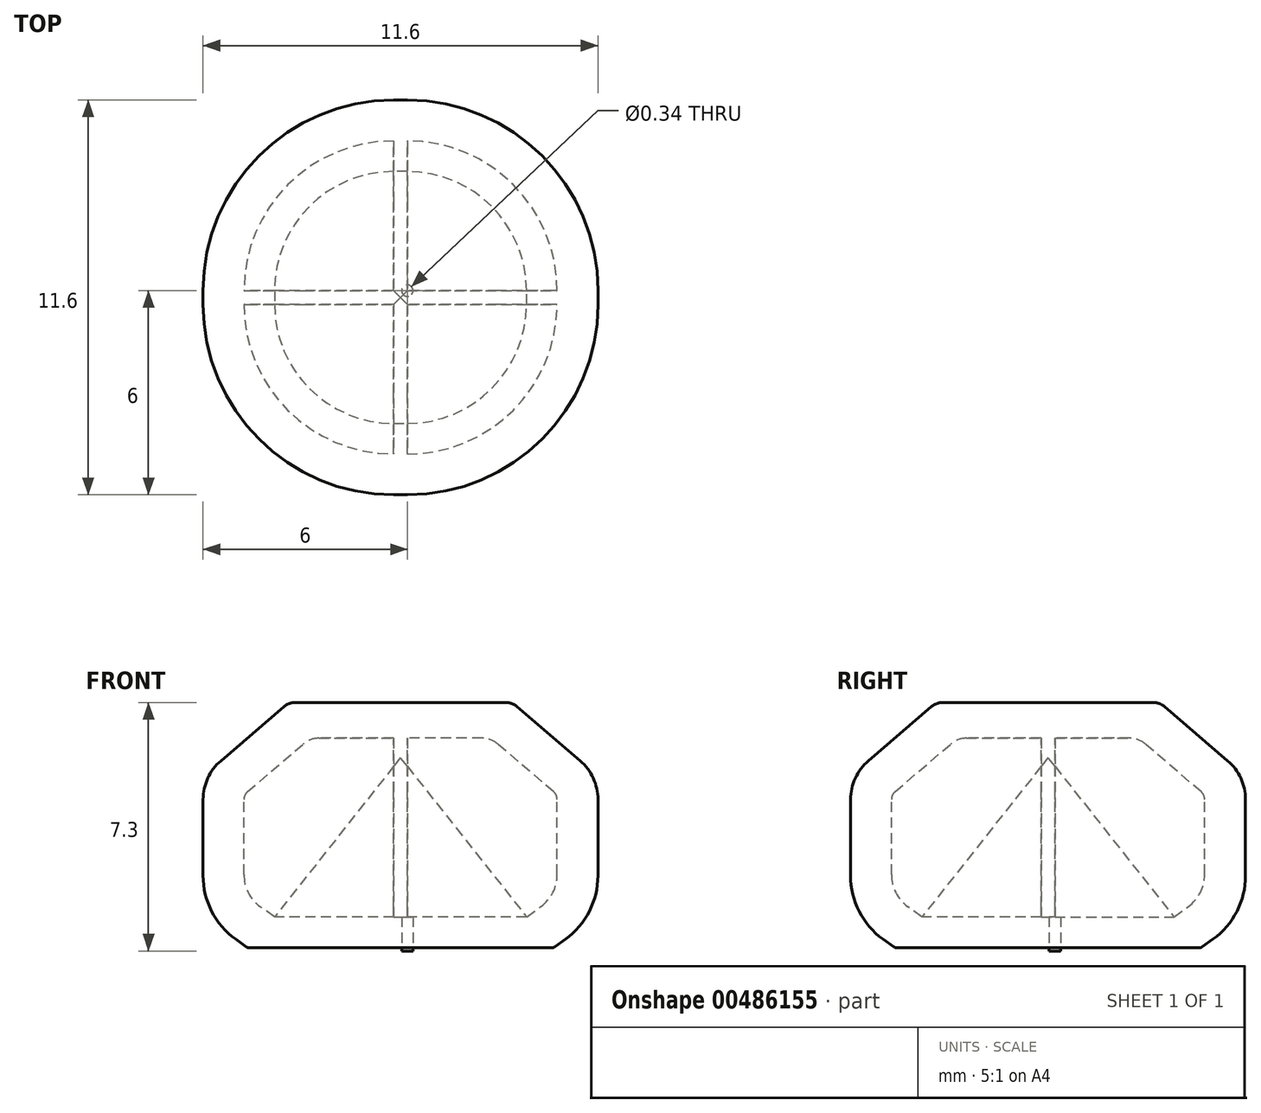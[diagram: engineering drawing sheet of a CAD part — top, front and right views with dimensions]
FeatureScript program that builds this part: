
annotation { "Feature Type Name" : "Feature", "Feature Type Description" : "" }
export const myFeature = defineFeature(function(context is Context, id is Id, definition is map)
    precondition{}
    {
        {
            assignVariable(context, id + "F0", {"name" : "l2", "anyValue" : 0.4});
        }
        {
            assignVariable(context, id + "F1", {"name" : "Scaf", "anyValue" : 0.65});
        }
        {
            var Q0;
            Q0=qCreatedBy(makeId("Front.planeOp"),FACE);
            var sketch = newSketch(context, id + "F2", { "sketchPlane" : qUnion([Q0])});
            skLineSegment(sketch, "E0", {"start": v(0, 0) * mm, "end": v(4.27, 0) * mm});
            skLineSegment(sketch, "E1", {"start": v(5.6, 2.11) * mm, "end": v(5.6, 4.35) * mm});
            skLineSegment(sketch, "E2", {"start": v(2.9, 7.2) * mm, "end": v(0, 7.2) * mm});
            skLineSegment(sketch, "E3", {"start": v(4.33, 0.02) * mm, "end": v(4.65, 0.25) * mm});
            skLineSegment(sketch, "E4", {"start": v(5.08, 5.49) * mm, "end": v(3.22, 7.08) * mm});
            skLineSegment(sketch, "E5", {"start": v(0, 0) * mm, "end": v(0, 0.9) * mm});
            skLineSegment(sketch, "E6", {"start": v(0, 0.9) * mm, "end": v(3.5, 0.9) * mm});
            skLineSegment(sketch, "E7", {"start": v(4.4, 2.14) * mm, "end": v(4.4, 4.35) * mm});
            skLineSegment(sketch, "E8", {"start": v(4.3, 4.58) * mm, "end": v(2.66, 5.98) * mm});
            skLineSegment(sketch, "E9", {"start": v(2.2, 6.15) * mm, "end": v(0, 6.15) * mm});
            skLineSegment(sketch, "E10", {"start": v(0, 6.15) * mm, "end": v(0, 7.2) * mm});
            skLineSegment(sketch, "E11", {"start": v(3.5, 0.9) * mm, "end": v(3.92, 1.2) * mm});
            skPoint(sketch, "E12.visualSharp", {"position": v(5.6, 0.94) * mm});
            skArc(sketch, "E12.filletArc", {"start": v(4.65, 0.25) * mm, "mid": v(5.35, 1.06) * mm, "end": v(5.6, 2.11) * mm});
            skPoint(sketch, "E13.visualSharp", {"position": v(5.6, 5.04) * mm});
            skArc(sketch, "E13.filletArc", {"start": v(5.6, 4.35) * mm, "mid": v(5.46, 4.98) * mm, "end": v(5.08, 5.49) * mm});
            skPoint(sketch, "E14.visualSharp", {"position": v(3.08, 7.2) * mm});
            skArc(sketch, "E14.filletArc", {"start": v(3.22, 7.08) * mm, "mid": v(3.07, 7.17) * mm, "end": v(2.9, 7.2) * mm});
            skPoint(sketch, "E15.visualSharp", {"position": v(2.46, 6.15) * mm});
            skArc(sketch, "E15.filletArc", {"start": v(2.66, 5.98) * mm, "mid": v(2.45, 6.1) * mm, "end": v(2.2, 6.15) * mm});
            skPoint(sketch, "E16.visualSharp", {"position": v(4.4, 4.49) * mm});
            skArc(sketch, "E16.filletArc", {"start": v(4.4, 4.35) * mm, "mid": v(4.37, 4.48) * mm, "end": v(4.3, 4.58) * mm});
            skPoint(sketch, "E17.visualSharp", {"position": v(4.4, 1.55) * mm});
            skArc(sketch, "E17.filletArc", {"start": v(3.92, 1.2) * mm, "mid": v(4.27, 1.61) * mm, "end": v(4.4, 2.14) * mm});
            skPoint(sketch, "E18.visualSharp", {"position": v(4.3, 0) * mm});
            skArc(sketch, "E18.filletArc", {"start": v(4.27, 0) * mm, "mid": v(4.3, 0) * mm, "end": v(4.33, 0.02) * mm});
            skSolve(sketch);
        }
        {
            var Q0;
            Q0=makeQuery(id+"F2.imprint","IMPRINT",FACE,{"disambiguationData":[TD([[makeQuery(id+"F2.imprint","IMPRINT",EDGE,{"derivedFrom":sQuery(id+"F2.wireOp",EDGE,"E0")}),1.0]])]});
            extrude(context, id + "F3", {"entities" : qUnion([Q0]), "depth" : (getVariable(context, 'l2')) * mm, "offsetDistance" : 25 * mm});
        }
        {
            var Q0;
            Q0=makeQuery(id+"F3.opExtrude","SWEPT_FACE",FACE,{"disambiguationData":[OSD([sQuery(id+"F2.wireOp",EDGE,"E10")])]});
            var Q1;
            Q1=sQuery(id+"F10.wireOp",EDGE,"E19");
            extrude(context, id + "F4", {"entities" : qUnion([Q0]), "operationType" : NewBodyOperationType.ADD, "surfaceEntities" : qUnion([Q1]), "depth" : (getVariable(context, 'Scaf')) * mm, "offsetDistance" : 25 * mm});
        }
        {
            var Q1;
            Q1=makeQuery(id+"F3.opExtrude","SWEPT_FACE",FACE,{"disambiguationData":[OSD([sQuery(id+"F2.wireOp",EDGE,"E9")])]});
            var Q2;
            Q2=makeQuery(id+"F3.opExtrude","SWEPT_FACE",FACE,{"disambiguationData":[OSD([sQuery(id+"F2.wireOp",EDGE,"E11")])]});
            loft(context, id + "F5", {"operationType" : NewBodyOperationType.ADD, "sheetProfilesArray" : [{ "sheetProfileEntities" : qUnion([Q1]) }, { "sheetProfileEntities" : qUnion([Q2]) }]});
        }
        {
            var Q1;
            Q1=makeQuery(id+"F3.opExtrude","SWEPT_FACE",FACE,{"disambiguationData":[OSD([sQuery(id+"F2.wireOp",EDGE,"E17.filletArc")])]});
            var Q2;
            Q2=makeQuery(id+"F3.opExtrude","SWEPT_FACE",FACE,{"disambiguationData":[OSD([sQuery(id+"F2.wireOp",EDGE,"E15.filletArc")])]});
            loft(context, id + "F6", {"operationType" : NewBodyOperationType.ADD, "sheetProfilesArray" : [{ "sheetProfileEntities" : qUnion([Q1]) }, { "sheetProfileEntities" : qUnion([Q2]) }]});
        }
        {
            var Q1;
            Q1=makeQuery(id+"F3.opExtrude","SWEPT_FACE",FACE,{"disambiguationData":[OSD([sQuery(id+"F2.wireOp",EDGE,"E8")])]});
            var Q2;
            Q2=makeQuery(id+"F3.opExtrude","SWEPT_FACE",FACE,{"disambiguationData":[OSD([sQuery(id+"F2.wireOp",EDGE,"E7")])]});
            loft(context, id + "F7", {"operationType" : NewBodyOperationType.ADD, "sheetProfilesArray" : [{ "sheetProfileEntities" : qUnion([Q1]) }, { "sheetProfileEntities" : qUnion([Q2]) }]});
        }
        {
            var Q0;
            Q0=makeQuery(id+"F7.opLoft","SWEPT_FACE",FACE,{"disambiguationData":[OSD([sQuery(id+"F2.wireOp",EDGE,"E7"),sQuery(id+"F2.wireOp",EDGE,"E8"),sQuery(id+"F2.wireOp",EDGE,"E16.filletArc")])]});
            extrude(context, id + "F8", {"entities" : qUnion([Q0]), "operationType" : NewBodyOperationType.ADD, "depth" : .2 * mm, "offsetDistance" : 25 * mm});
        }
        {
            var Q0;
            Q0=makeQuery(id+"F2.imprint","IMPRINT",FACE,{"disambiguationData":[TD([[makeQuery(id+"F2.imprint","IMPRINT",EDGE,{"derivedFrom":sQuery(id+"F2.wireOp",EDGE,"E0")}),1.0]])]});
            var Q1;
            Q1=sQuery(id+"F2.wireOp",EDGE,"E10");
            revolve(context, id + "F9", {"operationType" : NewBodyOperationType.ADD, "entities" : qUnion([Q0]), "axis" : qUnion([Q1]), "revolveType" : RevolveType.ONE_DIRECTION, "angle" : 90 * degree});
        }
        {
            var Q0;
            Q0=qCreatedBy(makeId("Front.planeOp"),FACE);
            var sketch = newSketch(context, id + "F10", { "sketchPlane" : qUnion([Q0])});
            skLineSegment(sketch, "E19", {"start": v(0, 0) * mm, "end": v(-0.4, 0) * mm});
            skLineSegment(sketch, "E20", {"start": v(-0.4, 0) * mm, "end": v(-0.4, 0.13) * mm});
            skSolve(sketch);
        }
        {
            var Q0;
            Q0=qCreatedBy(makeId("Front.planeOp"),FACE);
            cPlane(context, id + "F11", {"entities" : qUnion([Q0]), "cplaneType" : CPlaneType.OFFSET, "offset" : (getVariable(context, 'l2') / 2) * mm, "width" : 150 * mm, "height" : 150 * mm});
        }
        {
            var Q0;
            Q0=qCreatedBy(id+"F11.planeOp",FACE);
            var sketch = newSketch(context, id + "F12", { "sketchPlane" : qUnion([Q0])});
            skLineSegment(sketch, "E21", {"start": v(0, 0.03) * mm, "end": v(-0.2, 0.03) * mm});
            skLineSegment(sketch, "E22", {"start": v(-0.2, 0.03) * mm, "end": v(-0.2, 0.22) * mm});
            skLineSegment(sketch, "E23", {"start": v(0, 0.03) * mm, "end": v(0, 0.08) * mm});
            skLineSegment(sketch, "E24", {"start": v(0, 0.03) * mm, "end": v(0, 0.14) * mm});
            skPoint(sketch, "E24.endSnap0", {"position": v(0, 0.05) * mm});
            skSolve(sketch);
        }
        {
            var Q0;
            Q0=makeQuery(id+"F3.opExtrude","SWEPT_BODY",BODY,{"disambiguationData":[OSD([sQuery(id+"F2.wireOp",EDGE,"E0"),sQuery(id+"F2.wireOp",EDGE,"E1"),sQuery(id+"F2.wireOp",EDGE,"E2"),sQuery(id+"F2.wireOp",EDGE,"E3"),sQuery(id+"F2.wireOp",EDGE,"E4"),sQuery(id+"F2.wireOp",EDGE,"E5"),sQuery(id+"F2.wireOp",EDGE,"E6"),sQuery(id+"F2.wireOp",EDGE,"E7"),sQuery(id+"F2.wireOp",EDGE,"E8"),sQuery(id+"F2.wireOp",EDGE,"E9"),sQuery(id+"F2.wireOp",EDGE,"E10"),sQuery(id+"F2.wireOp",EDGE,"E11"),sQuery(id+"F2.wireOp",EDGE,"E12.filletArc"),sQuery(id+"F2.wireOp",EDGE,"E13.filletArc"),sQuery(id+"F2.wireOp",EDGE,"E14.filletArc"),sQuery(id+"F2.wireOp",EDGE,"E15.filletArc"),sQuery(id+"F2.wireOp",EDGE,"E16.filletArc"),sQuery(id+"F2.wireOp",EDGE,"E17.filletArc"),sQuery(id+"F2.wireOp",EDGE,"E18.filletArc")])]});
            var Q1;
            Q1=sQuery(id+"F12.wireOp",EDGE,"E22");
            transform(context, id + "F13", {"entities" : qUnion([Q0]), "transformType" : TransformType.ROTATION, "transformAxis" : qUnion([Q1]), "angle" : 90 * degree, "oppositeDirection" : true, "makeCopy" : true});
        }
        {
            var Q0;
            Q0=makeQuery(id+"F3.opExtrude","SWEPT_BODY",BODY,{"disambiguationData":[OSD([sQuery(id+"F2.wireOp",EDGE,"E0"),sQuery(id+"F2.wireOp",EDGE,"E1"),sQuery(id+"F2.wireOp",EDGE,"E2"),sQuery(id+"F2.wireOp",EDGE,"E3"),sQuery(id+"F2.wireOp",EDGE,"E4"),sQuery(id+"F2.wireOp",EDGE,"E5"),sQuery(id+"F2.wireOp",EDGE,"E6"),sQuery(id+"F2.wireOp",EDGE,"E7"),sQuery(id+"F2.wireOp",EDGE,"E8"),sQuery(id+"F2.wireOp",EDGE,"E9"),sQuery(id+"F2.wireOp",EDGE,"E10"),sQuery(id+"F2.wireOp",EDGE,"E11"),sQuery(id+"F2.wireOp",EDGE,"E12.filletArc"),sQuery(id+"F2.wireOp",EDGE,"E13.filletArc"),sQuery(id+"F2.wireOp",EDGE,"E14.filletArc"),sQuery(id+"F2.wireOp",EDGE,"E15.filletArc"),sQuery(id+"F2.wireOp",EDGE,"E16.filletArc"),sQuery(id+"F2.wireOp",EDGE,"E17.filletArc"),sQuery(id+"F2.wireOp",EDGE,"E18.filletArc")])]});
            var Q1;
            Q1=makeQuery(id+"F13.opPattern","COPY",BODY,{"derivedFrom":makeQuery(id+"F3.opExtrude","SWEPT_BODY",BODY,{"disambiguationData":[OSD([sQuery(id+"F2.wireOp",EDGE,"E0"),sQuery(id+"F2.wireOp",EDGE,"E1"),sQuery(id+"F2.wireOp",EDGE,"E2"),sQuery(id+"F2.wireOp",EDGE,"E3"),sQuery(id+"F2.wireOp",EDGE,"E4"),sQuery(id+"F2.wireOp",EDGE,"E5"),sQuery(id+"F2.wireOp",EDGE,"E6"),sQuery(id+"F2.wireOp",EDGE,"E7"),sQuery(id+"F2.wireOp",EDGE,"E8"),sQuery(id+"F2.wireOp",EDGE,"E9"),sQuery(id+"F2.wireOp",EDGE,"E10"),sQuery(id+"F2.wireOp",EDGE,"E11"),sQuery(id+"F2.wireOp",EDGE,"E12.filletArc"),sQuery(id+"F2.wireOp",EDGE,"E13.filletArc"),sQuery(id+"F2.wireOp",EDGE,"E14.filletArc"),sQuery(id+"F2.wireOp",EDGE,"E15.filletArc"),sQuery(id+"F2.wireOp",EDGE,"E16.filletArc"),sQuery(id+"F2.wireOp",EDGE,"E17.filletArc"),sQuery(id+"F2.wireOp",EDGE,"E18.filletArc")])]}),"instanceName":"1"});
            booleanBodies(context, id + "F14", {"operationType" : BooleanOperationType.UNION, "tools" : qUnion([Q0, Q1])});
        }
        {
            var Q0;
            Q0=makeQuery(id+"F3.opExtrude","SWEPT_BODY",BODY,{"disambiguationData":[OSD([sQuery(id+"F2.wireOp",EDGE,"E0"),sQuery(id+"F2.wireOp",EDGE,"E1"),sQuery(id+"F2.wireOp",EDGE,"E2"),sQuery(id+"F2.wireOp",EDGE,"E3"),sQuery(id+"F2.wireOp",EDGE,"E4"),sQuery(id+"F2.wireOp",EDGE,"E5"),sQuery(id+"F2.wireOp",EDGE,"E6"),sQuery(id+"F2.wireOp",EDGE,"E7"),sQuery(id+"F2.wireOp",EDGE,"E8"),sQuery(id+"F2.wireOp",EDGE,"E9"),sQuery(id+"F2.wireOp",EDGE,"E10"),sQuery(id+"F2.wireOp",EDGE,"E11"),sQuery(id+"F2.wireOp",EDGE,"E12.filletArc"),sQuery(id+"F2.wireOp",EDGE,"E13.filletArc"),sQuery(id+"F2.wireOp",EDGE,"E14.filletArc"),sQuery(id+"F2.wireOp",EDGE,"E15.filletArc"),sQuery(id+"F2.wireOp",EDGE,"E16.filletArc"),sQuery(id+"F2.wireOp",EDGE,"E17.filletArc"),sQuery(id+"F2.wireOp",EDGE,"E18.filletArc")])]});
            var Q1;
            Q1=sQuery(id+"F12.wireOp",EDGE,"E22");
            transform(context, id + "F15", {"entities" : qUnion([Q0]), "transformType" : TransformType.ROTATION, "transformAxis" : qUnion([Q1]), "angle" : 180 * degree, "makeCopy" : true});
        }
        {
            var Q0;
            Q0=makeQuery(id+"F3.opExtrude","SWEPT_BODY",BODY,{"disambiguationData":[OSD([sQuery(id+"F2.wireOp",EDGE,"E0"),sQuery(id+"F2.wireOp",EDGE,"E1"),sQuery(id+"F2.wireOp",EDGE,"E2"),sQuery(id+"F2.wireOp",EDGE,"E3"),sQuery(id+"F2.wireOp",EDGE,"E4"),sQuery(id+"F2.wireOp",EDGE,"E5"),sQuery(id+"F2.wireOp",EDGE,"E6"),sQuery(id+"F2.wireOp",EDGE,"E7"),sQuery(id+"F2.wireOp",EDGE,"E8"),sQuery(id+"F2.wireOp",EDGE,"E9"),sQuery(id+"F2.wireOp",EDGE,"E10"),sQuery(id+"F2.wireOp",EDGE,"E11"),sQuery(id+"F2.wireOp",EDGE,"E12.filletArc"),sQuery(id+"F2.wireOp",EDGE,"E13.filletArc"),sQuery(id+"F2.wireOp",EDGE,"E14.filletArc"),sQuery(id+"F2.wireOp",EDGE,"E15.filletArc"),sQuery(id+"F2.wireOp",EDGE,"E16.filletArc"),sQuery(id+"F2.wireOp",EDGE,"E17.filletArc"),sQuery(id+"F2.wireOp",EDGE,"E18.filletArc")])]});
            var Q1;
            Q1=makeQuery(id+"F15.opPattern","COPY",BODY,{"derivedFrom":makeQuery(id+"F3.opExtrude","SWEPT_BODY",BODY,{"disambiguationData":[OSD([sQuery(id+"F2.wireOp",EDGE,"E0"),sQuery(id+"F2.wireOp",EDGE,"E1"),sQuery(id+"F2.wireOp",EDGE,"E2"),sQuery(id+"F2.wireOp",EDGE,"E3"),sQuery(id+"F2.wireOp",EDGE,"E4"),sQuery(id+"F2.wireOp",EDGE,"E5"),sQuery(id+"F2.wireOp",EDGE,"E6"),sQuery(id+"F2.wireOp",EDGE,"E7"),sQuery(id+"F2.wireOp",EDGE,"E8"),sQuery(id+"F2.wireOp",EDGE,"E9"),sQuery(id+"F2.wireOp",EDGE,"E10"),sQuery(id+"F2.wireOp",EDGE,"E11"),sQuery(id+"F2.wireOp",EDGE,"E12.filletArc"),sQuery(id+"F2.wireOp",EDGE,"E13.filletArc"),sQuery(id+"F2.wireOp",EDGE,"E14.filletArc"),sQuery(id+"F2.wireOp",EDGE,"E15.filletArc"),sQuery(id+"F2.wireOp",EDGE,"E16.filletArc"),sQuery(id+"F2.wireOp",EDGE,"E17.filletArc"),sQuery(id+"F2.wireOp",EDGE,"E18.filletArc")])]}),"instanceName":"1"});
            booleanBodies(context, id + "F16", {"operationType" : BooleanOperationType.UNION, "tools" : qUnion([Q0, Q1])});
        }
        {
            var Q0;
            {var subQ0=sQuery(id+"F2.wireOp",EDGE,"E18.filletArc");var subQ1=sQuery(id+"F2.wireOp",EDGE,"E17.filletArc");var subQ2=sQuery(id+"F2.wireOp",EDGE,"E16.filletArc");var subQ3=sQuery(id+"F2.wireOp",EDGE,"E15.filletArc");var subQ4=sQuery(id+"F2.wireOp",EDGE,"E14.filletArc");var subQ5=sQuery(id+"F2.wireOp",EDGE,"E13.filletArc");var subQ6=sQuery(id+"F2.wireOp",EDGE,"E12.filletArc");var subQ7=sQuery(id+"F2.wireOp",EDGE,"E11");var subQ8=sQuery(id+"F2.wireOp",EDGE,"E10");var subQ9=sQuery(id+"F2.wireOp",EDGE,"E9");var subQ10=sQuery(id+"F2.wireOp",EDGE,"E8");var subQ11=sQuery(id+"F2.wireOp",EDGE,"E7");var subQ12=sQuery(id+"F2.wireOp",EDGE,"E6");var subQ13=sQuery(id+"F2.wireOp",EDGE,"E5");var subQ14=sQuery(id+"F2.wireOp",EDGE,"E4");var subQ15=sQuery(id+"F2.wireOp",EDGE,"E3");var subQ16=sQuery(id+"F2.wireOp",EDGE,"E2");var subQ17=sQuery(id+"F2.wireOp",EDGE,"E1");var subQ18=sQuery(id+"F2.wireOp",EDGE,"E0");var subQ19=makeQuery(id+"F9.opRevolve","CAP_FACE",FACE,{"disambiguationData":[OSD([subQ18,subQ17,subQ16,subQ15,subQ14,subQ13,subQ12,subQ11,subQ10,subQ9,subQ8,subQ7,subQ6,subQ5,subQ4,subQ3,subQ2,subQ1,subQ0])],"isStart":false});var subQ32=makeQuery(id+"F3.opExtrude","SWEPT_FACE",FACE,{"disambiguationData":[OSD([subQ13])]});var subQ33=makeQuery(id+"F3.opExtrude","SWEPT_FACE",FACE,{"disambiguationData":[OSD([subQ8])]});var subQ35=makeQuery(id+"F3.opExtrude","SWEPT_FACE",FACE,{"disambiguationData":[OSD([subQ16])]});Q0=makeQuery(id+"F15.opPattern","COPY",FACE,{"derivedFrom":makeQuery(id+"F14.opBoolean","SPLIT",FACE,{"disambiguationData":[TD([subQ35])],"derivedFrom":makeQuery(id+"F13.opPattern","COPY",FACE,{"derivedFrom":makeQuery(id+"F9.boolean.opBoolean","MERGE",FACE,{"derivedFrom":[subQ32,subQ33,subQ19]}),"instanceName":"1"})}),"instanceName":"1"});}
            extrude(context, id + "F17", {"entities" : qUnion([Q0]), "operationType" : NewBodyOperationType.ADD, "depth" : (getVariable(context, 'l2') * 1.5) * mm, "offsetDistance" : 25 * mm});
        }
        {
            var Q0;
            {var subQ0=sQuery(id+"F2.wireOp",EDGE,"E0");var subQ1=makeQuery(id+"F9.boolean.opBoolean","MERGE",FACE,{"derivedFrom":[makeQuery(id+"F3.opExtrude","SWEPT_FACE",FACE,{"disambiguationData":[OSD([subQ0])]}),makeQuery(id+"F9.opRevolve","SWEPT_FACE",FACE,{"disambiguationData":[OSD([subQ0])]})]});var subQ2=makeQuery(id+"F14.opBoolean","MERGE",FACE,{"derivedFrom":[subQ1,makeQuery(id+"F13.opPattern","COPY",FACE,{"derivedFrom":subQ1,"instanceName":"1"})]});Q0=makeQuery(id+"F17.boolean.opBoolean","MERGE",FACE,{"derivedFrom":[makeQuery(id+"F16.opBoolean","MERGE",FACE,{"derivedFrom":[subQ2,makeQuery(id+"F15.opPattern","COPY",FACE,{"derivedFrom":subQ2,"instanceName":"1"})]}),makeQuery(id+"F17.opExtrude","SWEPT_FACE",FACE,{"disambiguationData":[OSD([subQ0,sQuery(id+"F2.wireOp",EDGE,"E5")])]})]});}
            var sketch = newSketch(context, id + "F18", { "sketchPlane" : qUnion([Q0])});
            skCircle(sketch, "E25", {"center": v(0, 0) * mm, "radius": 0.17 * mm});
            skSolve(sketch);
        }
        {
            var Q0;
            Q0=makeQuery(id+"F18.imprint","IMPRINT",FACE,{"disambiguationData":[TD([[makeQuery(id+"F18.imprint","IMPRINT",EDGE,{"derivedFrom":sQuery(id+"F18.wireOp",EDGE,"E25")}),-1.0]])]});
            cPlane(context, id + "F19", {"entities" : qUnion([Q0]), "cplaneType" : CPlaneType.OFFSET, "offset" : .1 * mm, "width" : 150 * mm, "height" : 150 * mm});
        }
        {
            var Q0;
            Q0=qCreatedBy(id+"F19.planeOp",FACE);
            var sketch = newSketch(context, id + "F20", { "sketchPlane" : qUnion([Q0])});
            skLineSegment(sketch, "E26", {"start": v(0, 0) * mm, "end": v(-0.33, -0.11) * mm});
            skSolve(sketch);
        }
        {
            var Q0;
            Q0=makeQuery(id+"F18.imprint","IMPRINT",FACE,{"disambiguationData":[TD([[makeQuery(id+"F18.imprint","IMPRINT",EDGE,{"derivedFrom":sQuery(id+"F18.wireOp",EDGE,"E25")}),1.0]])]});
            extrude(context, id + "F21", {"entities" : qUnion([Q0]), "operationType" : NewBodyOperationType.ADD, "depth" : .1 * mm, "offsetDistance" : 25 * mm});
        }
        {
            var Q1;
            Q1=makeQuery(id+"F18.imprint","IMPRINT",FACE,{"disambiguationData":[TD([[makeQuery(id+"F18.imprint","IMPRINT",EDGE,{"derivedFrom":sQuery(id+"F18.wireOp",EDGE,"E25")}),1.0]])]});
            var Q2;
            Q2=sQuery(id+"F20.wireOp",VERTEX,"E26.start");
            loft(context, id + "F22", {"operationType" : NewBodyOperationType.ADD, "sheetProfilesArray" : [{ "sheetProfileEntities" : qUnion([Q1]) }, { "sheetProfileEntities" : qUnion([Q2]) }]});
        }
        {
            var Q0;
            Q0=makeQuery(id+"F18.imprint","IMPRINT",FACE,{"disambiguationData":[TD([[makeQuery(id+"F18.imprint","IMPRINT",EDGE,{"derivedFrom":sQuery(id+"F18.wireOp",EDGE,"E25")}),1.0]])]});
            extrude(context, id + "F23", {"entities" : qUnion([Q0]), "operationType" : NewBodyOperationType.REMOVE, "oppositeDirection" : true, "depth" : 1 * mm, "offsetDistance" : 25 * mm});
        }
    });
